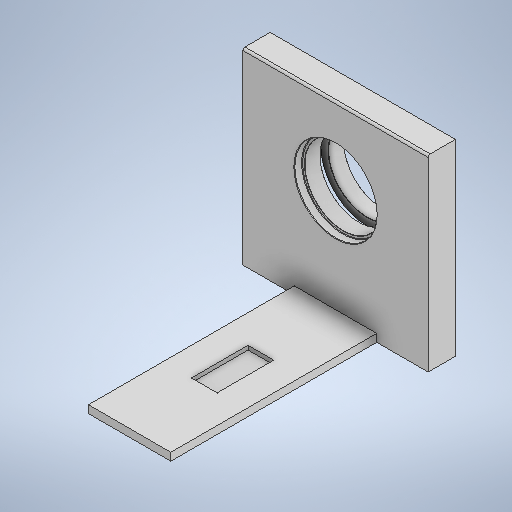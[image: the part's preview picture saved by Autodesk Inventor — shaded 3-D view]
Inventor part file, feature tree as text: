
AUTODESK INVENTOR PART (.ipt)
format: ipt  version: 2025.2 (Build 292293000, 293)  size: 411,136 bytes
history: native  units: in
note: dims shown in document units (in); Inventor stores cm internally (conversion verified against a paired STEP export)
features: sketch x10, fillet x9, extrude x8, plane x4, revolve x1
ambient origin geometry x8: Origin, YZ Plane, XZ Plane, XY Plane, X Axis, Y Axis, Z Axis, Center Point
bodies: Solid1 (feature_tree)
feature tree (32):
  extrude  "Extrusion1"  Depth=29.5276in
  plane  "Work Plane1"
  extrude  "Extrusion2"  Depth=5.9055in TaperAngle=0.0deg
  plane  "Work Plane2"
  revolve  "Revolution1"  [1 undecoded]
  plane  "Work Plane3"
  plane  "Work Plane4"
  extrude  "Extrusion5"  Depth=0.3937in
  fillet  "Fillet1"  [1 undecoded]
  fillet  "Fillet2"  Radius=0.5906in
  fillet  "Fillet3"  Radius=0.3937in
  fillet  "Fillet4"  Radius=1.5748in
  fillet  "Fillet5"  [1 undecoded]
  fillet  "Fillet6"  Radius=31.4961in
  fillet  "Fillet7"  Radius=70.8661in
  fillet  "Fillet8"  Radius=59.0551in
  fillet  "Fillet9"  Radius=2.9528in
  extrude  "Extrusion7"  Depth=0.1969in
  extrude  "Extrusion8"  Depth=0.0787in
  extrude  "Extrusion9"  Depth=0.0787in
  extrude  "Extrusion10"  Depth=0.0787in
  extrude  "Extrusion11"  Depth=12.7953in TaperAngle=0.0deg
  sketch  "Sketch1"  dims[d0=29.5276in d2=35.4331in]
  sketch  "Sketch2"  dims[d8=15.748in d10=3.1496in]
  sketch  "Sketch5"  dims[d11=0.5906in d12=0.3937in d13=360.0deg d14=0.5906in d15=0.3937in d16=1.5748in d32=0.0in d33=31.4961in d34=70.8661in d35=59.0551in d36=2.9528in d37=0.0in]
  sketch  "Sketch11"  dims[d48=0.1969in d49=0.1969in]
  sketch  "Sketch15"  dims[d50=0.0787in d51=0.0787in]
  sketch  "Sketch16"  dims[d52=0.0787in d53=0.0787in]
  sketch  "Sketch17"  dims[d54=0.0787in d55=0.0787in]
  sketch  "Sketch18"  dims[d56=0.7874in d60=12.7953in d61=0.0in]
  sketch  "Sketch20"  dims[d64=15.748in d65=2.9528in d66=31.4961in d67=78.7402in d68=0.0in d72=28.5433in d73=1.5748in d74=0.0in d81=7.4803in d82=0.0in d84=1.1811in d86=3.937in d87=0.3937in d89=0.3937in d92=7.4803in d93=0.0in d59=0.0in d62=0.0in]
  sketch  "Sketch Rectangular Pattern1"  dims[d3=5.9055in d4=0.0in d6=5.9055in d7=0.0in]
note: 3 required parameter values undecoded (feature->parameter linkage not recoverable at this tier; creation-order binding heuristic only, values carry confidence <= 0.55)